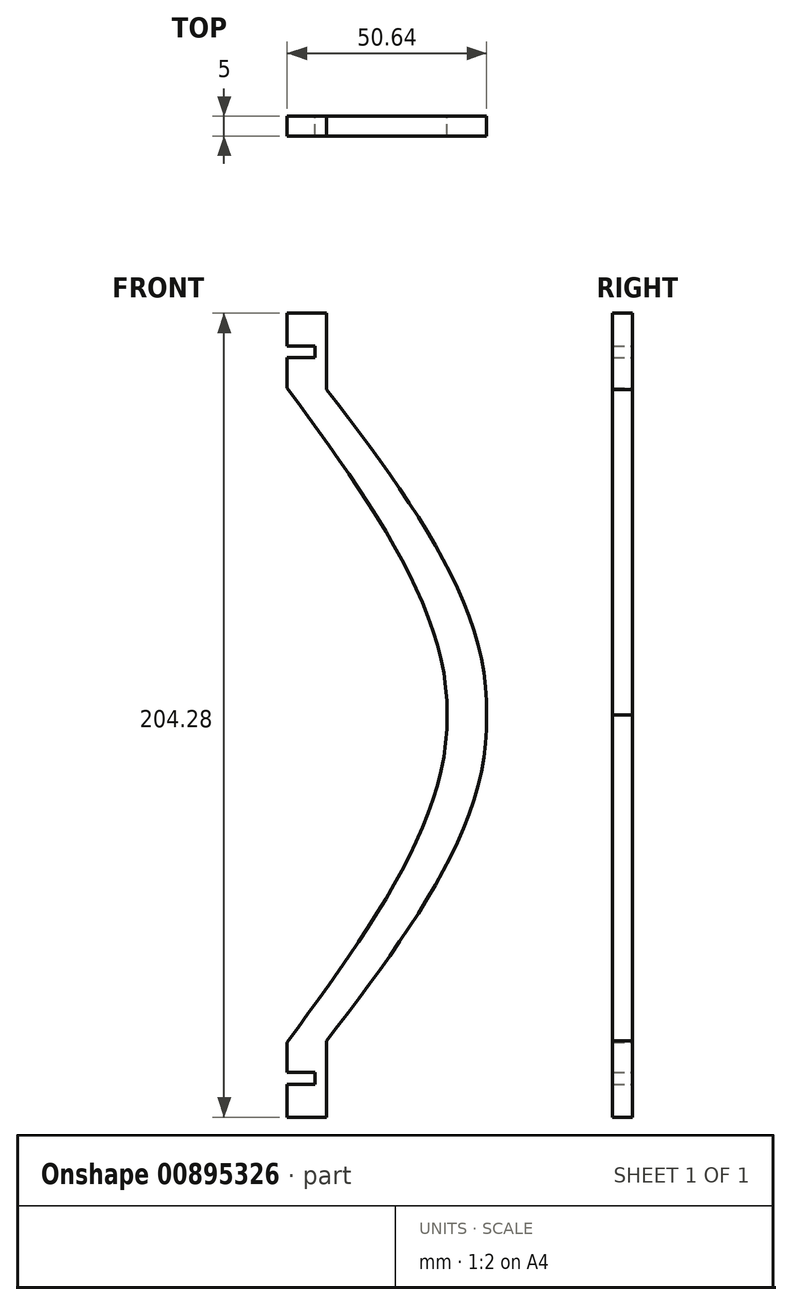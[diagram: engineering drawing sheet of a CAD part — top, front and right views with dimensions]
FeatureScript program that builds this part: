
annotation { "Feature Type Name" : "Feature", "Feature Type Description" : "" }
export const myFeature = defineFeature(function(context is Context, id is Id, definition is map)
    precondition{}
    {
        {
            var Q0;
            Q0=qCreatedBy(makeId("Front.planeOp"),FACE);
            var sketch = newSketch(context, id + "F0", { "sketchPlane" : qUnion([Q0])});
            skLineSegment(sketch, "E0", {"start": v(0, 83.14) * mm, "end": v(0, 90.81) * mm});
            skLineSegment(sketch, "E1", {"start": v(0, 102.14) * mm, "end": v(10, 102.14) * mm});
            skLineSegment(sketch, "E2", {"start": v(10, 102.14) * mm, "end": v(10, 82.71) * mm});
            skFitSpline(sketch, "E3", {"points": [v(10, 82.71) * mm, v(50.6, 0) * mm, v(0, -86.07) * mm], "startDerivative": vector(129.87, -168.84) * mm, "endDerivative": vector(-148, -168.73) * mm});
            skFitSpline(sketch, "E4", {"points": [v(0, 83.14) * mm, v(40.6, 0) * mm, v(0, -76.07) * mm], "startDerivative": vector(120.97, -165.4) * mm, "endDerivative": vector(-122.79, -149.25) * mm});
            skLineSegment(sketch, "E5", {"start": v(7, 93.81) * mm, "end": v(7, 90.81) * mm});
            skLineSegment(sketch, "E6", {"start": v(7, 90.81) * mm, "end": v(0, 90.81) * mm});
            skLineSegment(sketch, "E7.trimOffspring", {"start": v(0, 93.81) * mm, "end": v(0, 102.14) * mm});
            skFitSpline(sketch, "E8.MirrorCS", {"points": [v(0, -83.14) * mm, v(40.6, 0) * mm, v(0, 76.07) * mm], "startDerivative": vector(120.97, 165.4) * mm, "endDerivative": vector(-122.79, 149.25) * mm});
            skFitSpline(sketch, "E9.MirrorCS", {"points": [v(10, -82.71) * mm, v(50.6, 0) * mm, v(0, 86.07) * mm], "startDerivative": vector(129.87, 168.84) * mm, "endDerivative": vector(-148, 168.73) * mm});
            skLineSegment(sketch, "E10.MirrorCS", {"start": v(0, -93.81) * mm, "end": v(0, -102.14) * mm});
            skLineSegment(sketch, "E11.MirrorCS", {"start": v(0, -102.14) * mm, "end": v(10, -102.14) * mm});
            skLineSegment(sketch, "E12.MirrorCS", {"start": v(10, -102.14) * mm, "end": v(10, -82.71) * mm});
            skLineSegment(sketch, "E13.MirrorCS", {"start": v(0, -83.14) * mm, "end": v(0, -90.81) * mm});
            skLineSegment(sketch, "E14.MirrorCS", {"start": v(7, -90.81) * mm, "end": v(0, -90.81) * mm});
            skLineSegment(sketch, "E15.MirrorCS", {"start": v(7, -93.81) * mm, "end": v(7, -90.81) * mm});
            skLineSegment(sketch, "E16", {"start": v(0, 93.81) * mm, "end": v(7, 93.81) * mm});
            skLineSegment(sketch, "E17.MirrorCS", {"start": v(0, -93.81) * mm, "end": v(7, -93.81) * mm});
            skLineSegment(sketch, "E18", {"start": v(0, 0) * mm, "end": v(40.6, 0) * mm});
            skLineSegment(sketch, "E19", {"start": v(50.6, 0) * mm, "end": v(40.6, 0) * mm});
            skSolve(sketch);
        }
        {
            var Q0;
            Q0 = qSketchRegion(id + "F0", true);
            extrude(context, id + "F1", {"entities" : qUnion([Q0]), "depth" : 5 * mm, "offsetDistance" : 25 * mm});
        }
    });
